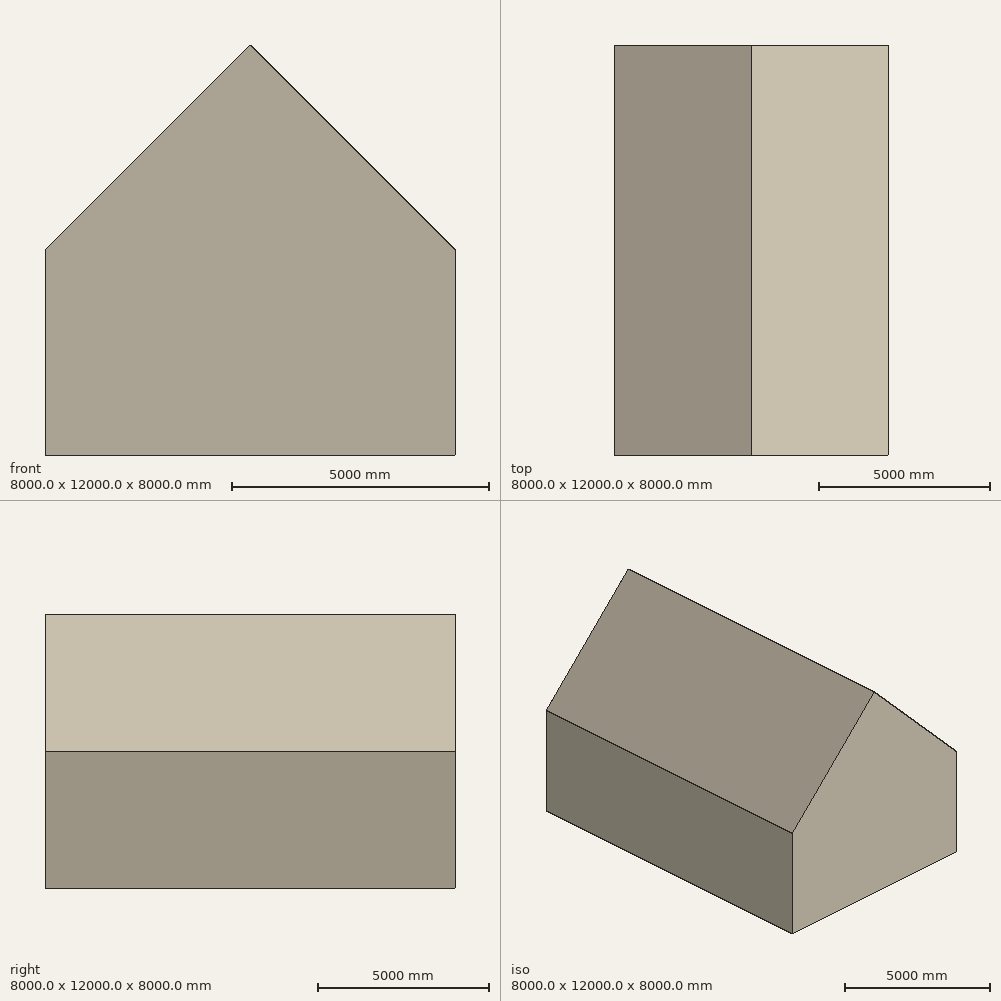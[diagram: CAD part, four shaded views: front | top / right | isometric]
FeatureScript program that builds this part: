
annotation { "Feature Type Name" : "Feature", "Feature Type Description" : "" }
export const myFeature = defineFeature(function(context is Context, id is Id, definition is map)
    precondition{}
    {
        {
            var Q0;
            Q0=qCreatedBy(makeId("Front.planeOp"),FACE);
            var sketch = newSketch(context, id + "F0", { "sketchPlane" : qUnion([Q0])});
            skLineSegment(sketch, "E0", {"start": v(0, 0) * mm, "end": v(8000, 0) * mm});
            skLineSegment(sketch, "E1", {"start": v(8000, 0) * mm, "end": v(8000, 4000) * mm});
            skLineSegment(sketch, "E2", {"start": v(0, 0) * mm, "end": v(0, 4000) * mm});
            skLineSegment(sketch, "E3", {"start": v(4000, 0) * mm, "end": v(4000, 8000) * mm, "construction": true});
            skLineSegment(sketch, "E4", {"start": v(0, 4000) * mm, "end": v(4000, 8000) * mm});
            skLineSegment(sketch, "E5", {"start": v(4000, 8000) * mm, "end": v(8000, 4000) * mm});
            skSolve(sketch);
        }
        {
            var Q0;
            Q0=makeQuery(id+"F0.imprint","IMPRINT",FACE,{"disambiguationData":[TD([[makeQuery(id+"F0.imprint","IMPRINT",EDGE,{"derivedFrom":sQuery(id+"F0.wireOp",EDGE,"E0")}),1.0]])]});
            extrude(context, id + "F1", {"entities" : qUnion([Q0]), "oppositeDirection" : true, "depth" : 12000 * mm});
        }
    });
